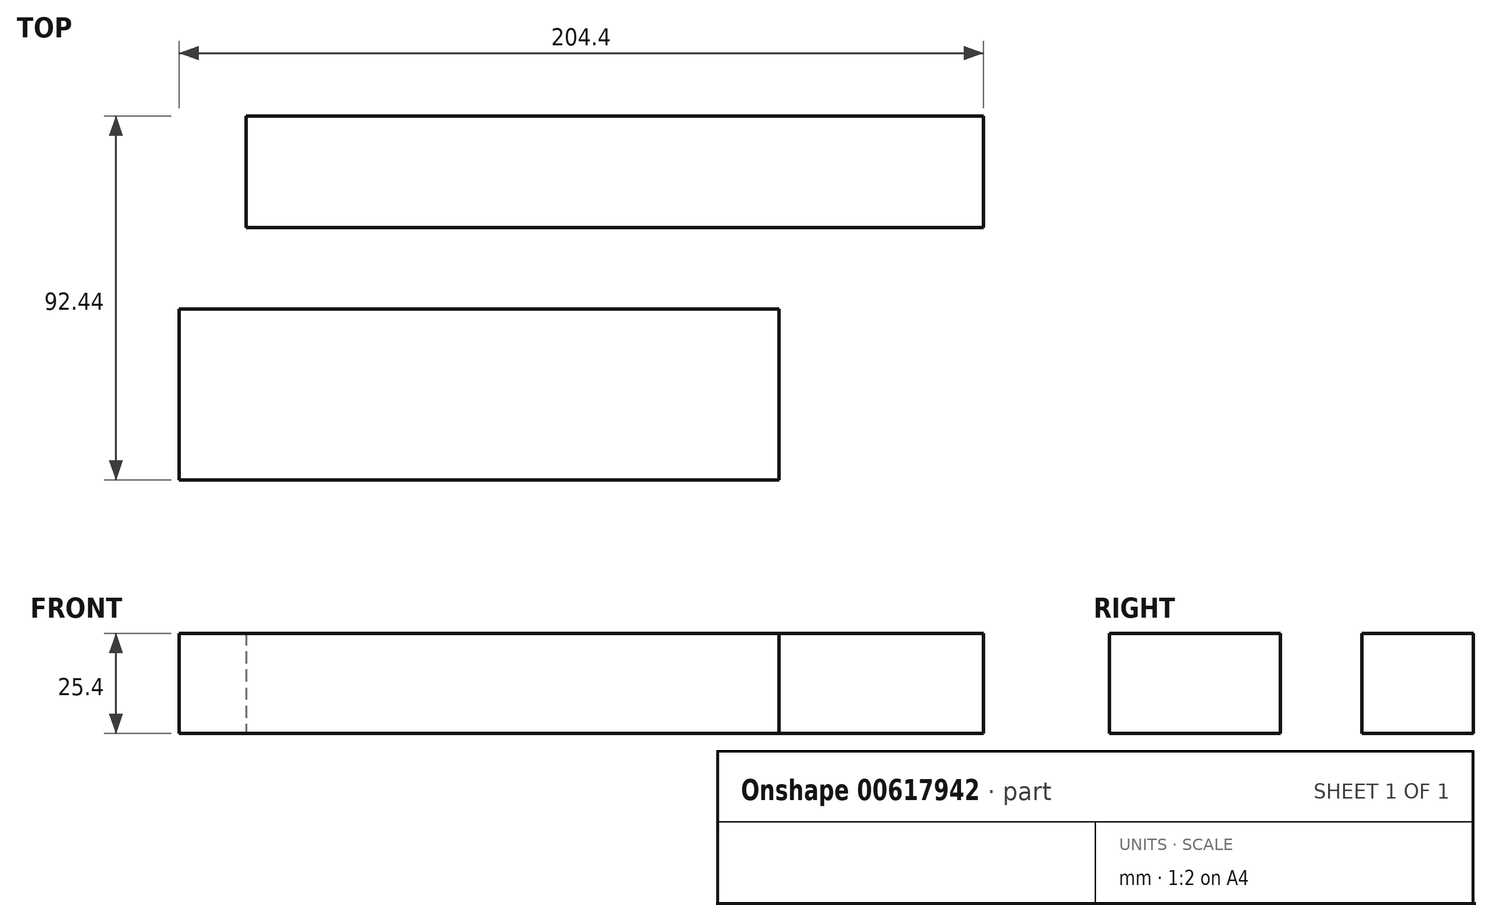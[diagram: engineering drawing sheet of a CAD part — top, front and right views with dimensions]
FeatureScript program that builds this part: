
annotation { "Feature Type Name" : "Feature", "Feature Type Description" : "" }
export const myFeature = defineFeature(function(context is Context, id is Id, definition is map)
    precondition{}
    {
        {
            var Q0;
            Q0=qCreatedBy(makeId("Top.planeOp"),FACE);
            var sketch = newSketch(context, id + "F0", { "sketchPlane" : qUnion([Q0])});
            skLineSegment(sketch, "E0.bottom", {"start": v(-75.75, 11.6) * mm, "end": v(76.65, 11.6) * mm});
            skLineSegment(sketch, "E0.top", {"start": v(-75.75, -31.88) * mm, "end": v(76.65, -31.88) * mm});
            skLineSegment(sketch, "E0.left", {"start": v(-75.75, 11.6) * mm, "end": v(-75.75, -31.88) * mm});
            skLineSegment(sketch, "E0.right", {"start": v(76.65, 11.6) * mm, "end": v(76.65, -31.88) * mm});
            skLineSegment(sketch, "E1.bottom", {"start": v(128.65, 32.26) * mm, "end": v(-58.68, 32.26) * mm});
            skLineSegment(sketch, "E1.top", {"start": v(128.65, 60.56) * mm, "end": v(-58.68, 60.56) * mm});
            skLineSegment(sketch, "E1.left", {"start": v(128.65, 32.26) * mm, "end": v(128.65, 60.56) * mm});
            skLineSegment(sketch, "E1.right", {"start": v(-58.68, 32.26) * mm, "end": v(-58.68, 60.56) * mm});
            skSolve(sketch);
        }
        {
            var Q0;
            Q0=makeQuery(id+"F0.imprint","IMPRINT",FACE,{"disambiguationData":[TD([[makeQuery(id+"F0.imprint","IMPRINT",EDGE,{"derivedFrom":sQuery(id+"F0.wireOp",EDGE,"E1.bottom")}),-1.0]])]});
            var Q1;
            Q1=makeQuery(id+"F0.imprint","IMPRINT",FACE,{"disambiguationData":[TD([[makeQuery(id+"F0.imprint","IMPRINT",EDGE,{"derivedFrom":sQuery(id+"F0.wireOp",EDGE,"E0.bottom")}),-1.0]])]});
            extrude(context, id + "F1", {"entities" : qUnion([Q0, Q1]), "depth" : 25.4 * mm, "offsetDistance" : 25.4 * mm});
        }
    });
